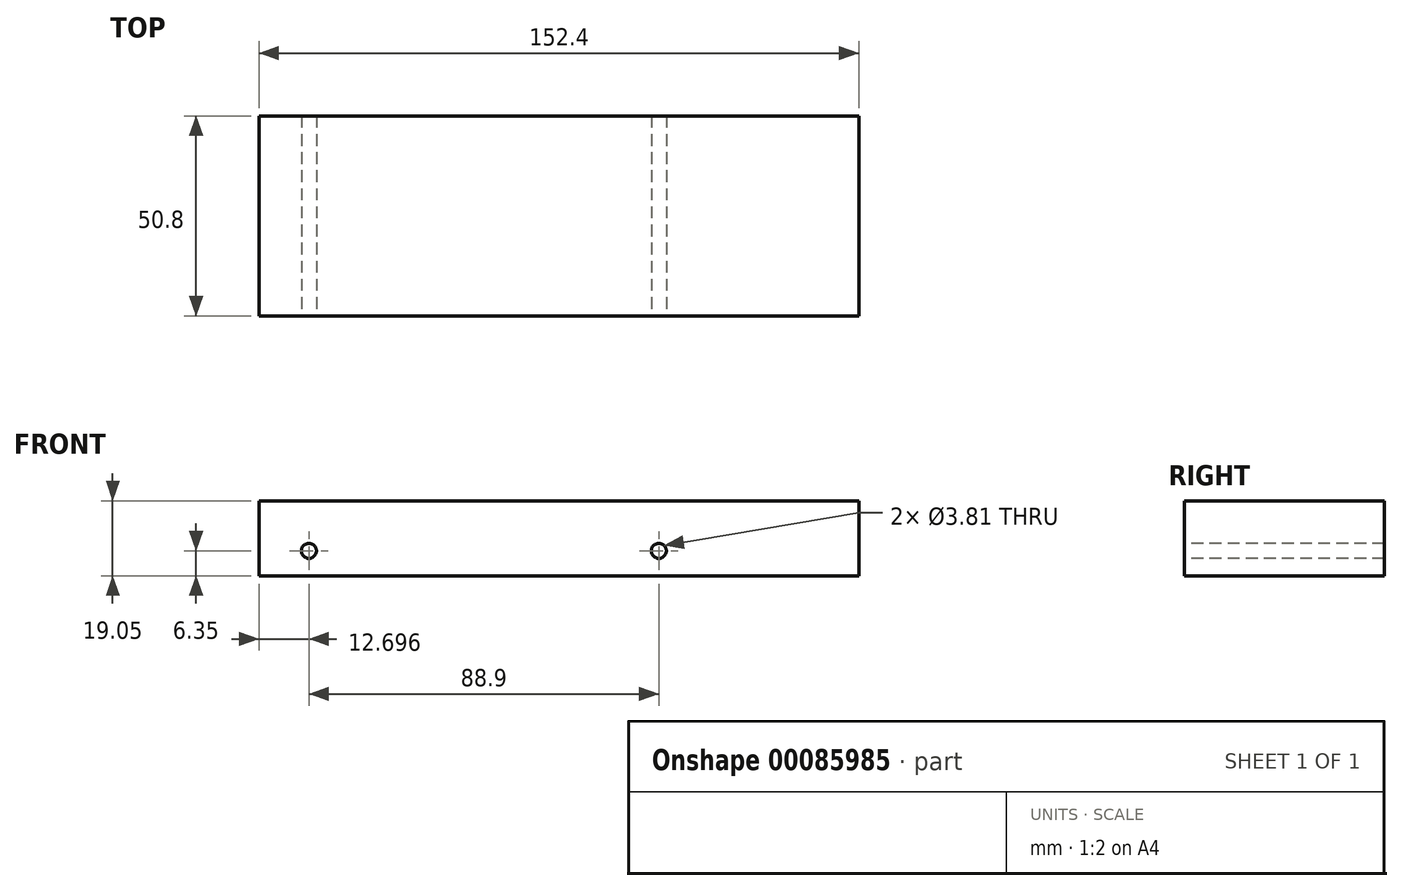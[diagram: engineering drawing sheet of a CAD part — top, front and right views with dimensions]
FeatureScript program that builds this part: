
annotation { "Feature Type Name" : "Feature", "Feature Type Description" : "" }
export const myFeature = defineFeature(function(context is Context, id is Id, definition is map)
    precondition{}
    {
        {
            var Q0;
            Q0=qCreatedBy(makeId("Top.planeOp"),FACE);
            var sketch = newSketch(context, id + "F0", { "sketchPlane" : qUnion([Q0])});
            skLineSegment(sketch, "E0.bottom", {"start": v(-46.1, 0) * mm, "end": v(106.3, 0) * mm});
            skLineSegment(sketch, "E0.top", {"start": v(-46.1, 50.8) * mm, "end": v(106.3, 50.8) * mm});
            skLineSegment(sketch, "E0.left", {"start": v(-46.1, 0) * mm, "end": v(-46.1, 50.8) * mm});
            skLineSegment(sketch, "E0.right", {"start": v(106.3, 0) * mm, "end": v(106.3, 50.8) * mm});
            skPoint(sketch, "E1", {"position": v(55.5, 50.8) * mm});
            skPoint(sketch, "E2", {"position": v(106.3, 25.4) * mm});
            skLineSegment(sketch, "E3", {"start": v(55.5, 50.8) * mm, "end": v(55.5, 25.4) * mm});
            skLineSegment(sketch, "E4", {"start": v(55.5, 25.4) * mm, "end": v(106.3, 25.4) * mm});
            skSolve(sketch);
        }
        {
            var Q0;
            Q0 = qSketchRegion(id + "F0", true);
            extrude(context, id + "F1", {"entities" : qUnion([Q0]), "depth" : 19.05 * mm});
        }
        {
            var Q0;
            Q0=makeQuery(id+"F1.opExtrude","SWEPT_FACE",FACE,{"disambiguationData":[OSD([sQuery(id+"F0.wireOp",EDGE,"E0.bottom")])]});
            var sketch = newSketch(context, id + "F2", { "sketchPlane" : qUnion([Q0])});
            skCircle(sketch, "E5", {"center": v(-33.4, 6.35) * mm, "radius": 1.9 * mm});
            skCircle(sketch, "E6", {"center": v(55.5, 6.35) * mm, "radius": 1.9 * mm});
            skSolve(sketch);
        }
        {
            var Q0;
            Q0=makeQuery(id+"F2.imprint","IMPRINT",FACE,{"disambiguationData":[TD([[makeQuery(id+"F2.imprint","IMPRINT",EDGE,{"derivedFrom":sQuery(id+"F2.wireOp",EDGE,"E5")}),1.0]])]});
            var Q1;
            Q1=makeQuery(id+"F2.imprint","IMPRINT",FACE,{"disambiguationData":[TD([[makeQuery(id+"F2.imprint","IMPRINT",EDGE,{"derivedFrom":sQuery(id+"F2.wireOp",EDGE,"E6")}),1.0]])]});
            extrude(context, id + "F3", {"entities" : qUnion([Q0, Q1]), "operationType" : NewBodyOperationType.REMOVE, "oppositeDirection" : true, "depth" : 76.2 * mm});
        }
    });
